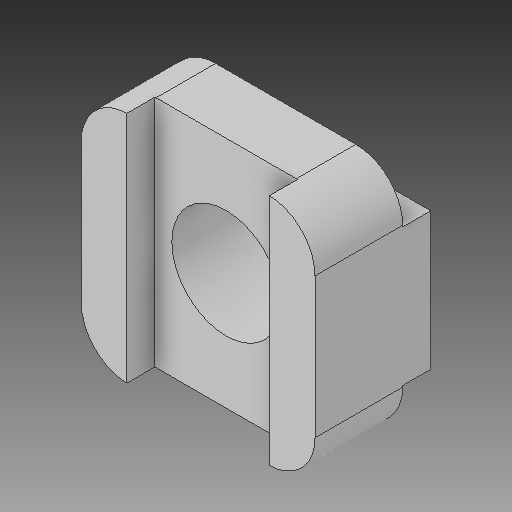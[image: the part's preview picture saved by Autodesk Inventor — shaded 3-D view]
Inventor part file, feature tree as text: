
AUTODESK INVENTOR PART (.ipt)
format: ipt  version: 2018 (Build 220112000, 112)  size: 139,264 bytes
history: native  units: in
note: dims shown in document units (in); Inventor stores cm internally (conversion verified against a paired STEP export)
features: extrude x3, sketch x3, fillet x1
ambient origin geometry x8: Origin, YZ Plane, XZ Plane, XY Plane, X Axis, Y Axis, Z Axis, Center Point
bodies: Solid1 (feature_tree)
feature tree (7):
  extrude  "Extrusion1"  Depth=1.5748in
  extrude  "Extrusion2"  Depth=0.9252in
  fillet  "Fillet1"  Radius=1.5748in
  extrude  "Extrusion3"  Depth=0.189in
  sketch  "Sketch1"  dims[d0=0.5906in d1=1.5748in]
  sketch  "Sketch2"  dims[d2=0.189in d3=0.9252in d4=1.5748in d5=0.0in]
  sketch  "Sketch3"  dims[d6=0.9606in d7=0.189in d8=1.5748in d9=0.0in d10=0.315in d11=0.7323in d12=1.5748in d13=0.0in]
